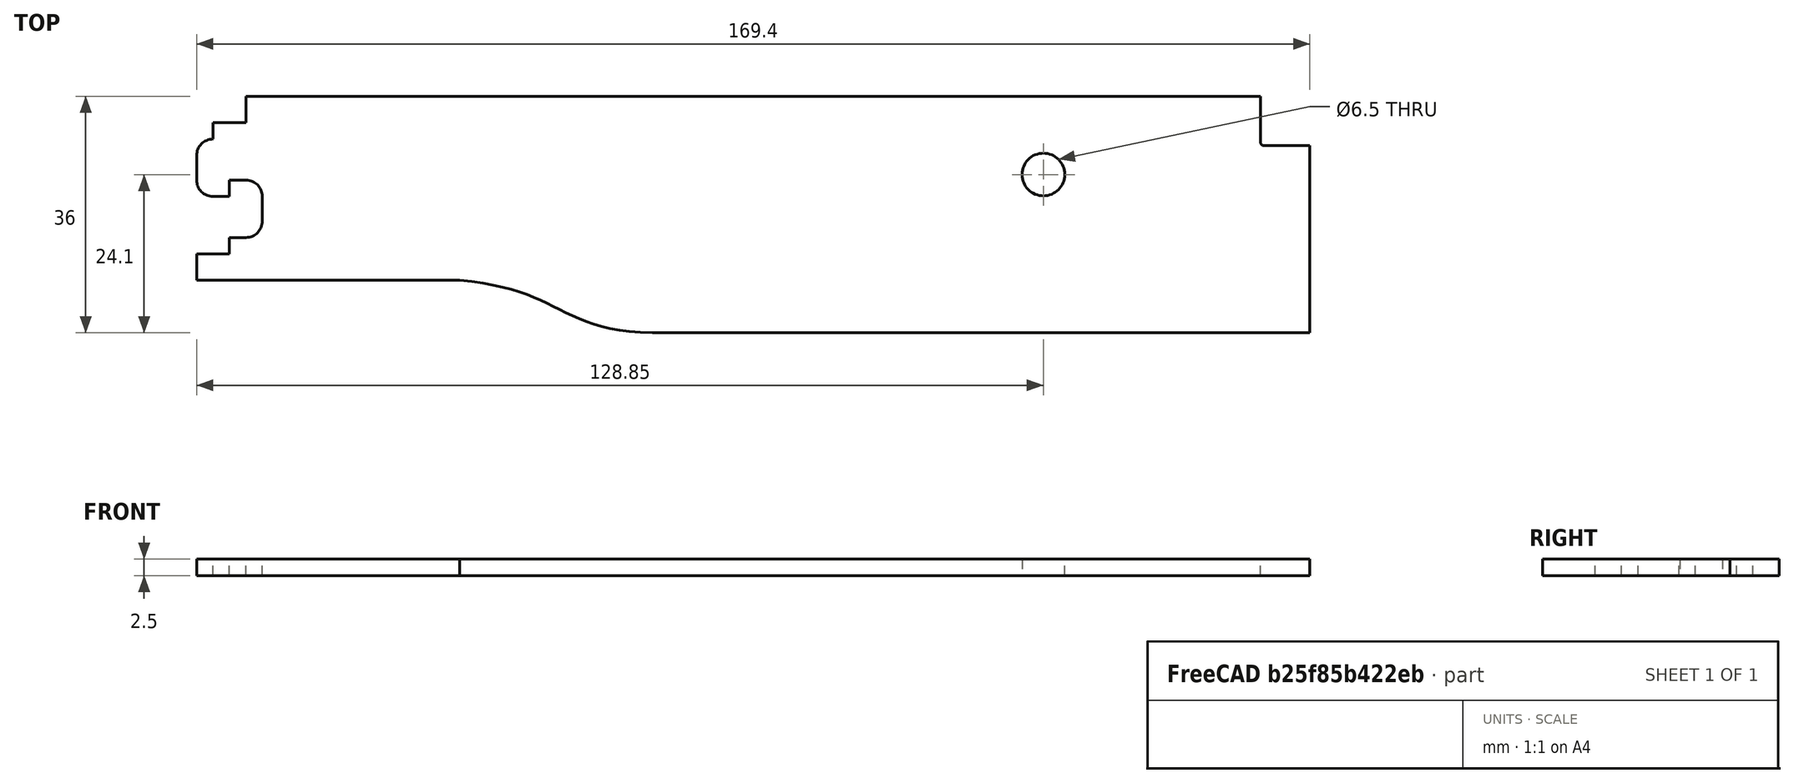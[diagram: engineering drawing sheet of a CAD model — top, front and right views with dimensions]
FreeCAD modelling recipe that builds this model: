
FCSTD DOCUMENT  (FreeCAD 0.19R0.19.2)
Label: v0_10
License: All rights reserved
LicenseURL: http://en.wikipedia.org/wiki/All_rights_reserved
objects: Part::Extrusion×2, Sketcher::SketchObject×1
note: 3 computed .brp shape members not serialized (recipe doc carries the construction recipe); baked Part::Feature solids carry a one-line shape summary decoded from their .brp

FEATURE [Sketcher::SketchObject] Sketch
  FullyConstrained = true
  sketch-geometry (33):
    g0: LineSegment StartX=0 StartY=0 StartZ=0 EndX=154.4 EndY=0 EndZ=0
    g1: LineSegment StartX=154.4 StartY=0 StartZ=0 EndX=154.4 EndY=-7 EndZ=0
    g2: LineSegment StartX=154.9 StartY=-7.5 StartZ=0 EndX=161.9 EndY=-7.5 EndZ=0
    g3: ArcOfCircle CenterX=154.9 CenterY=-7 CenterZ=0 NormalX=0 NormalY=0 NormalZ=1 AngleXU=0 Radius=0.5 StartAngle=3.14159 EndAngle=4.71239
    g4: Circle CenterX=121.35 CenterY=-11.9 CenterZ=0 NormalX=0 NormalY=0 NormalZ=1 AngleXU=0 Radius=3.25
    g5: LineSegment StartX=0 StartY=0 StartZ=0 EndX=0 EndY=-4 EndZ=0
    g6: LineSegment StartX=-5 StartY=-4 StartZ=0 EndX=0 EndY=-4 EndZ=0
    g7: LineSegment StartX=-5 StartY=-4 StartZ=0 EndX=-5 EndY=-6.5 EndZ=0
    g8: LineSegment StartX=-7.5 StartY=-9 StartZ=0 EndX=-7.5 EndY=-12.75 EndZ=0
    g9: ArcOfCircle CenterX=-5 CenterY=-9 CenterZ=0 NormalX=0 NormalY=0 NormalZ=1 AngleXU=0 Radius=2.5 StartAngle=1.5708 EndAngle=3.14159
    g10: LineSegment StartX=-5 StartY=-15.25 StartZ=0 EndX=-2.5 EndY=-15.25 EndZ=0
    g11: ArcOfCircle CenterX=-5 CenterY=-12.75 CenterZ=0 NormalX=0 NormalY=0 NormalZ=1 AngleXU=0 Radius=2.5 StartAngle=3.14159 EndAngle=4.71239
    g12: LineSegment StartX=-2.5 StartY=-15.25 StartZ=0 EndX=-2.5 EndY=-12.75 EndZ=0
    g13: LineSegment StartX=-2.5 StartY=-12.75 StartZ=0 EndX=1.488e-13 EndY=-12.75 EndZ=0
    g14: ArcOfCircle CenterX=1.486e-13 CenterY=-15.25 CenterZ=0 NormalX=0 NormalY=0 NormalZ=1 AngleXU=0 Radius=2.5 StartAngle=8e-16 EndAngle=1.5708
    g15: LineSegment StartX=2.5 StartY=-15.25 StartZ=0 EndX=2.5 EndY=-19 EndZ=0
    g16: ArcOfCircle CenterX=1.483e-13 CenterY=-19 CenterZ=0 NormalX=0 NormalY=0 NormalZ=1 AngleXU=0 Radius=2.5 StartAngle=4.71239 EndAngle=6.28319
    g17: LineSegment StartX=-2.5 StartY=-21.5 StartZ=0 EndX=1.479e-13 EndY=-21.5 EndZ=0
    g18: LineSegment StartX=-2.5 StartY=-21.5 StartZ=0 EndX=-2.5 EndY=-24 EndZ=0
    g19: LineSegment StartX=-7.5 StartY=-24 StartZ=0 EndX=-2.5 EndY=-24 EndZ=0
    g20: LineSegment StartX=-7.5 StartY=-24 StartZ=0 EndX=-7.5 EndY=-28 EndZ=0
    g21: LineSegment StartX=161.9 StartY=-7.5 StartZ=0 EndX=161.9 EndY=-36 EndZ=0
    g22: LineSegment StartX=61.85 StartY=-36 StartZ=0 EndX=161.9 EndY=-36 EndZ=0
    g23-g27: Circle x5 (B-spline internal-alignment scaffolding for g28; pole/knot coordinates omitted)
    g28: BSplineCurve PolesCount=5 KnotsCount=3 Degree=3 IsPeriodic=0
    g29: GeomPoint X=61.85 Y=-36 Z=0
    g30: GeomPoint X=47.2264 Y=-32.2128 Z=0
    g31: GeomPoint X=32.5209 Y=-28 Z=0
    g32: LineSegment StartX=32.5209 StartY=-28 StartZ=0 EndX=-7.5 EndY=-28 EndZ=0
  constraints (75):
    c: PointOnObject(g0,g-2)
    c: Horizontal(g0)
    c: Distance(g0) = 154.4
    c: DistanceY(g-1,g0) = 0
    c: Vertical(g1)
    c: Distance(g1) = 7
    c: Coincident(g1,g0)
    c: Horizontal(g2)
    c: Distance(g2) = 7
    c: Coincident(g3,g1)
    c: Tangent(g2,g3)
    c: Tangent(g2,g3,g2) = -1.5708
    c: Block(g3)
    c: Block(g4)
    c: Vertical(g5)
    c: Distance(g5) = 4
    c: Coincident(g5,g0)
    c: Horizontal(g6)
    c: Distance(g6) = 5
    c: Coincident(g6,g5)
    c: Vertical(g7)
    c: Distance(g7) = 2.5
    c: Coincident(g7,g6)
    c: Vertical(g8)
    c: Distance(g8) = 3.75
    c: Coincident(g9,g7)
    c: Block(g9)
    c: Coincident(g8,g9)
    c: Horizontal(g10)
    c: Distance(g10) = 2.5
    c: Coincident(g11,g8)
    c: Block(g11)
    c: Block(g10)
    c: Vertical(g12)
    c: Distance(g12) = 2.5
    c: Coincident(g12,g10)
    c: Horizontal(g13)
    c: Distance(g13) = 2.5
    c: Coincident(g13,g12)
    c: Coincident(g14,g13)
    c: Vertical(g15)
    c: Distance(g15) = 3.75
    c: Block(g14)
    c: Coincident(g15,g14)
    c: Coincident(g16,g15)
    c: Block(g16)
    c: Horizontal(g17)
    c: Distance(g17) = 2.5
    c: Coincident(g17,g16)
    c: Vertical(g18)
    c: Distance(g18) = 2.5
    c: Coincident(g18,g17)
    c: Horizontal(g19)
    c: Distance(g19) = 5
    c: Coincident(g19,g18)
    c: Vertical(g20)
    c: Distance(g20) = 4
    c: Coincident(g20,g19)
    c: Vertical(g21)
    c: Distance(g21) = 28.5
    c: Coincident(g21,g2)
    c: Horizontal(g22)
    c: Distance(g22) = 100.05
    c: Coincident(g22,g21)
    c: Coincident(g28,g22)
    c: Weight(g23) = 1
    c: Equal(g23, g24-g27) x4
    c: InternalAlignment(g23-g27 -> g28) x5
    c: InternalAlignment(g29,g28)
    c: InternalAlignment(g30,g28)
    c: InternalAlignment(g31,g28)
    c: Horizontal(g32)
    c: Coincident(g32,g20)
    c: Coincident(g32,g28)
    c: Block(g28)
FEATURE [Part::Extrusion] Extrude
  Base = -> Sketch
  Dir = (0,0,1)
  DirMode = 2
  FaceMakerClass = Part::FaceMakerBullseye
  LengthFwd = 2.5
  LengthRev = 0
  Solid = true
  Symmetric = false
FEATURE [Part::Extrusion] Extrude001
  Base = -> Sketch
  Dir = (0,0,1)
  DirMode = 2
  FaceMakerClass = Part::FaceMakerBullseye
  LengthFwd = 2.5
  LengthRev = 0
  Solid = true
  Symmetric = false
